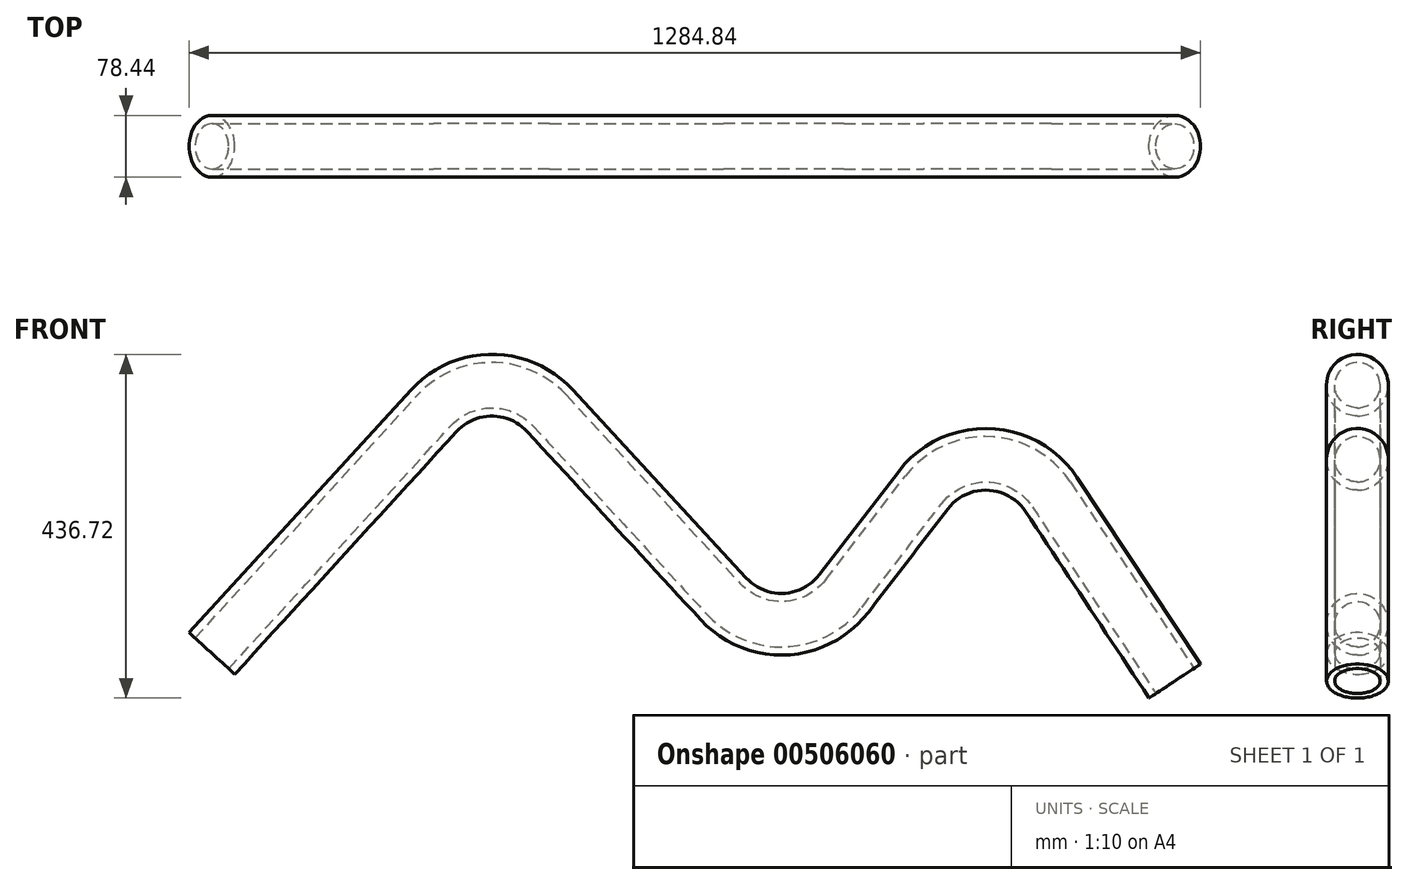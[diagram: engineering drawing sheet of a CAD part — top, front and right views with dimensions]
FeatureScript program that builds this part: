
annotation { "Feature Type Name" : "Feature", "Feature Type Description" : "" }
export const myFeature = defineFeature(function(context is Context, id is Id, definition is map)
    precondition{}
    {
        {
            var Q0;
            Q0=qCreatedBy(makeId("Front.planeOp"),FACE);
            var sketch = newSketch(context, id + "F0", { "sketchPlane" : qUnion([Q0])});
            skLineSegment(sketch, "E0", {"start": v(-719.55, -179.99) * mm, "end": v(-437.78, 128.28) * mm});
            skLineSegment(sketch, "E1", {"start": v(-290.46, 128.62) * mm, "end": v(-69.68, -110.71) * mm});
            skLineSegment(sketch, "E2", {"start": v(83.12, -103.82) * mm, "end": v(184.08, 27.6) * mm});
            skLineSegment(sketch, "E3", {"start": v(346.77, 21.9) * mm, "end": v(503.64, -215.04) * mm});
            skPoint(sketch, "E4.visualSharp", {"position": v(-364.3, 208.66) * mm});
            skArc(sketch, "E4.filletArc", {"start": v(-290.46, 128.62) * mm, "mid": v(-364.2, 160.81) * mm, "end": v(-437.78, 128.28) * mm});
            skPoint(sketch, "E5.visualSharp", {"position": v(10.81, -197.97) * mm});
            skArc(sketch, "E5.filletArc", {"start": v(-69.68, -110.71) * mm, "mid": v(8.32, -142.8) * mm, "end": v(83.12, -103.82) * mm});
            skPoint(sketch, "E6.visualSharp", {"position": v(269.42, 138.72) * mm});
            skArc(sketch, "E6.filletArc", {"start": v(346.77, 21.9) * mm, "mid": v(266.9, 66.63) * mm, "end": v(184.08, 27.6) * mm});
            skSolve(sketch);
        }
        {
            var Q0;
            Q0=sQuery(id+"F0.wireOp",VERTEX,"E0.start");
            var Q1;
            Q1=sQuery(id+"F0.wireOp",EDGE,"E0");
            cPlane(context, id + "F1", {"entities" : qUnion([Q0, Q1]), "cplaneType" : CPlaneType.LINE_POINT, "offset" : 25 * mm, "width" : 150 * mm, "height" : 150 * mm});
        }
        {
            var Q0;
            Q0=qCreatedBy(id+"F1.planeOp",FACE);
            var sketch = newSketch(context, id + "F2", { "sketchPlane" : qUnion([Q0])});
            skPoint(sketch, "E7.0", {"position": v(-409.67, 0) * mm});
            skCircle(sketch, "E8", {"center": v(-409.67, 0) * mm, "radius": 39.22 * mm});
            skCircle(sketch, "E9", {"center": v(-409.67, 0) * mm, "radius": 28.8 * mm});
            skSolve(sketch);
        }
        {
            var Q0;
            Q0=makeQuery(id+"F2.imprint","IMPRINT",FACE,{"disambiguationData":[TD([[makeQuery(id+"F2.imprint","IMPRINT",EDGE,{"derivedFrom":sQuery(id+"F2.wireOp",EDGE,"E8")}),1.0]])]});
            var Q1;
            Q1 = qConstructionFilter(qBodyType(qCreatedBy(id + "F0" ,EDGE), BodyType.WIRE), ConstructionObject.NO);
            sweep(context, id + "F3", {"profiles" : qUnion([Q0]), "path" : qUnion([Q1])});
        }
    });
